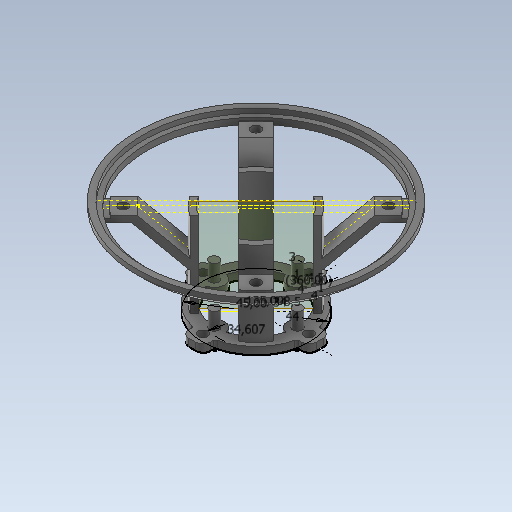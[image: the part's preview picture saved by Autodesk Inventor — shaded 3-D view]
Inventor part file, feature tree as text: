
AUTODESK INVENTOR PART (.ipt)
format: ipt  version: 2020 (Build 240168000, 168)  size: 603,136 bytes
history: native  units: mm
features: projected_geometry x28, sketch x16, extrude x9, other x5, pattern_circular x1, sweep x1
ambient origin geometry x8: Origin, YZ Plane, XZ Plane, XY Plane, X Axis, Y Axis, Z Axis, Center Point
bodies: Body1 (feature_tree)
feature tree (60):
  other  "Твердое тело1"
  sketch  "Эскиз1"
  extrude  "Выдавливание1"  Depth=44.0mm
  extrude  "Выдавливание2"  Depth=4.0mm
  sketch  "Эскиз3"
  extrude  "Выдавливание4"  Depth=40.0mm TaperAngle=360.0deg
  pattern_circular  "Круговой массив1"  [2 undecoded]
  other  "РабПлоскость2"
  sketch  "Эскиз5"
  other  "РабПлоскость1"
  sketch  "Эскиз6"
  sketch  "Эскиз7"
  extrude  "Выдавливание6"  Depth=4.5mm
  sketch  "Эскиз8"
  extrude  "Выдавливание7"  Depth=3.0mm
  sketch  "Эскиз9"
  other  "РабПлоскость3"
  sketch  "Эскиз10"
  sweep  "Сдвиг1"
  extrude  "Выдавливание8"  Depth=1.0mm
  extrude  "Выдавливание9"  TaperAngle=45.0deg  [1 undecoded]
  sketch  "Эскиз14"
  other  "РабПлоскость4"
  sketch  "Эскиз15"
  extrude  "Выдавливание10"  TaperAngle=135.0deg  [1 undecoded]
  extrude  "Выдавливание11"  Depth=34.0mm
  sketch  "Эскиз2"
  sketch  "Эскиз4"
  projected_geometry  "Спроецированная петля1"
  projected_geometry  "Спроецированная петля2"
  projected_geometry  "Спроецированная петля3"
  projected_geometry  "Спроецированная петля4"
  projected_geometry  "Спроецированная петля5"
  projected_geometry  "Спроецированная петля6"
  projected_geometry  "Спроецированная петля7"
  projected_geometry  "Спроецированная петля8"
  projected_geometry  "Спроецированная петля9"
  projected_geometry  "Спроецированная петля10"
  projected_geometry  "Спроецированная петля11"
  projected_geometry  "Спроецированная петля12"
  projected_geometry  "Спроецированная петля13"
  projected_geometry  "Спроецированная петля14"
  projected_geometry  "Спроецированная петля15"
  projected_geometry  "Спроецированная петля16"
  projected_geometry  "Спроецированная петля17"
  projected_geometry  "Спроецированная петля18"
  projected_geometry  "Спроецированная петля19"
  projected_geometry  "Спроецированная петля20"
  sketch  "Эскиз11"
  projected_geometry  "Спроецированная петля21"
  projected_geometry  "Спроецированная петля22"
  projected_geometry  "Спроецированная петля23"
  sketch  "3D эскиз1"
  sketch  "Эскиз12"
  sketch  "Эскиз13"
  projected_geometry  "Спроецированная петля24"
  projected_geometry  "Спроецированная петля25"
  projected_geometry  "Спроецированная петля26"
  projected_geometry  "Спроецированная петля27"
  projected_geometry  "Спроецированная петля28"
note: 4 required parameter values undecoded (feature->parameter linkage not recoverable at this tier; creation-order binding heuristic only, values carry confidence <= 0.55)
